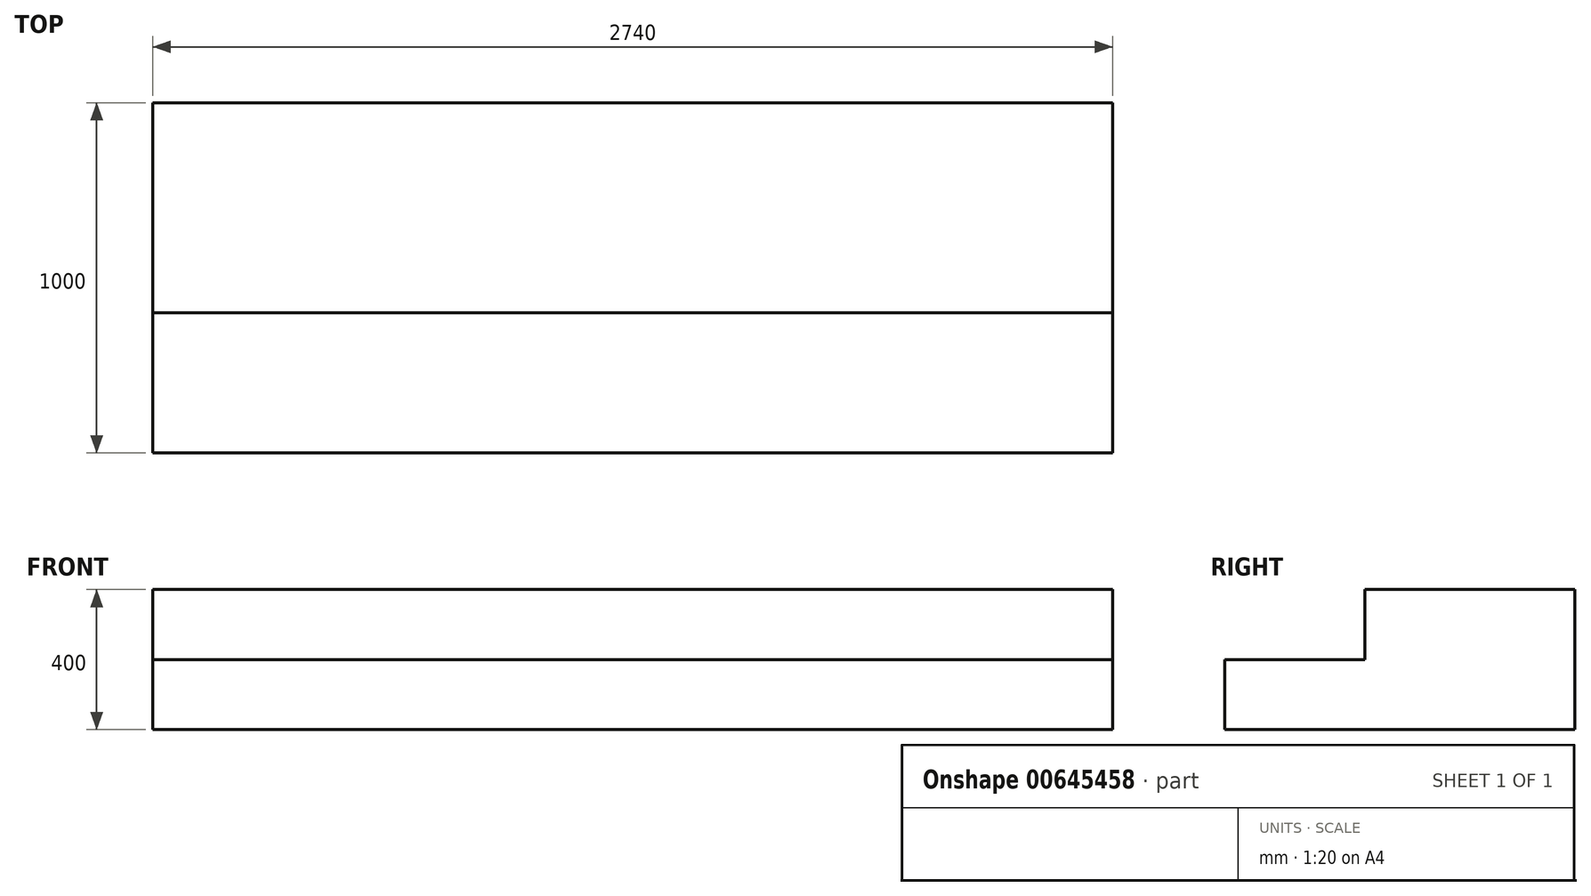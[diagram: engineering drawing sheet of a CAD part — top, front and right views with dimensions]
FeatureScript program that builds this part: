
annotation { "Feature Type Name" : "Feature", "Feature Type Description" : "" }
export const myFeature = defineFeature(function(context is Context, id is Id, definition is map)
    precondition{}
    {
        {
            var Q0;
            Q0=qCreatedBy(makeId("Top.planeOp"),FACE);
            var sketch = newSketch(context, id + "F0", { "sketchPlane" : qUnion([Q0])});
            skLineSegment(sketch, "E0", {"start": v(0, 0) * mm, "end": v(-2740, 0) * mm});
            skLineSegment(sketch, "E1", {"start": v(-2740, 400) * mm, "end": v(0, 400) * mm});
            skLineSegment(sketch, "E2", {"start": v(0, 1000) * mm, "end": v(0, 0) * mm});
            skLineSegment(sketch, "E3", {"start": v(0, 400) * mm, "end": v(0, 0) * mm});
            skLineSegment(sketch, "E4", {"start": v(-2740, 0) * mm, "end": v(-2740, 400) * mm});
            skLineSegment(sketch, "E5", {"start": v(0, 1000) * mm, "end": v(-2740, 1000) * mm});
            skLineSegment(sketch, "E6", {"start": v(-2740, 1000) * mm, "end": v(-2740, 400) * mm});
            skSolve(sketch);
        }
        {
            var Q0;
            Q0=makeQuery(id+"F0.imprint","IMPRINT",FACE,{"disambiguationData":[TD([[makeQuery(id+"F0.imprint","IMPRINT",EDGE,{"derivedFrom":sQuery(id+"F0.wireOp",EDGE,"E1")}),1.0]])]});
            extrude(context, id + "F1", {"entities" : qUnion([Q0]), "depth" : 400 * mm, "offsetDistance" : 25 * mm});
        }
        {
            var Q0;
            Q0=makeQuery(id+"F0.imprint","IMPRINT",FACE,{"disambiguationData":[TD([[makeQuery(id+"F0.imprint","IMPRINT",EDGE,{"derivedFrom":sQuery(id+"F0.wireOp",EDGE,"E0")}),-1.0]])]});
            extrude(context, id + "F2", {"entities" : qUnion([Q0]), "operationType" : NewBodyOperationType.ADD, "depth" : 200 * mm, "offsetDistance" : 25 * mm});
        }
    });
